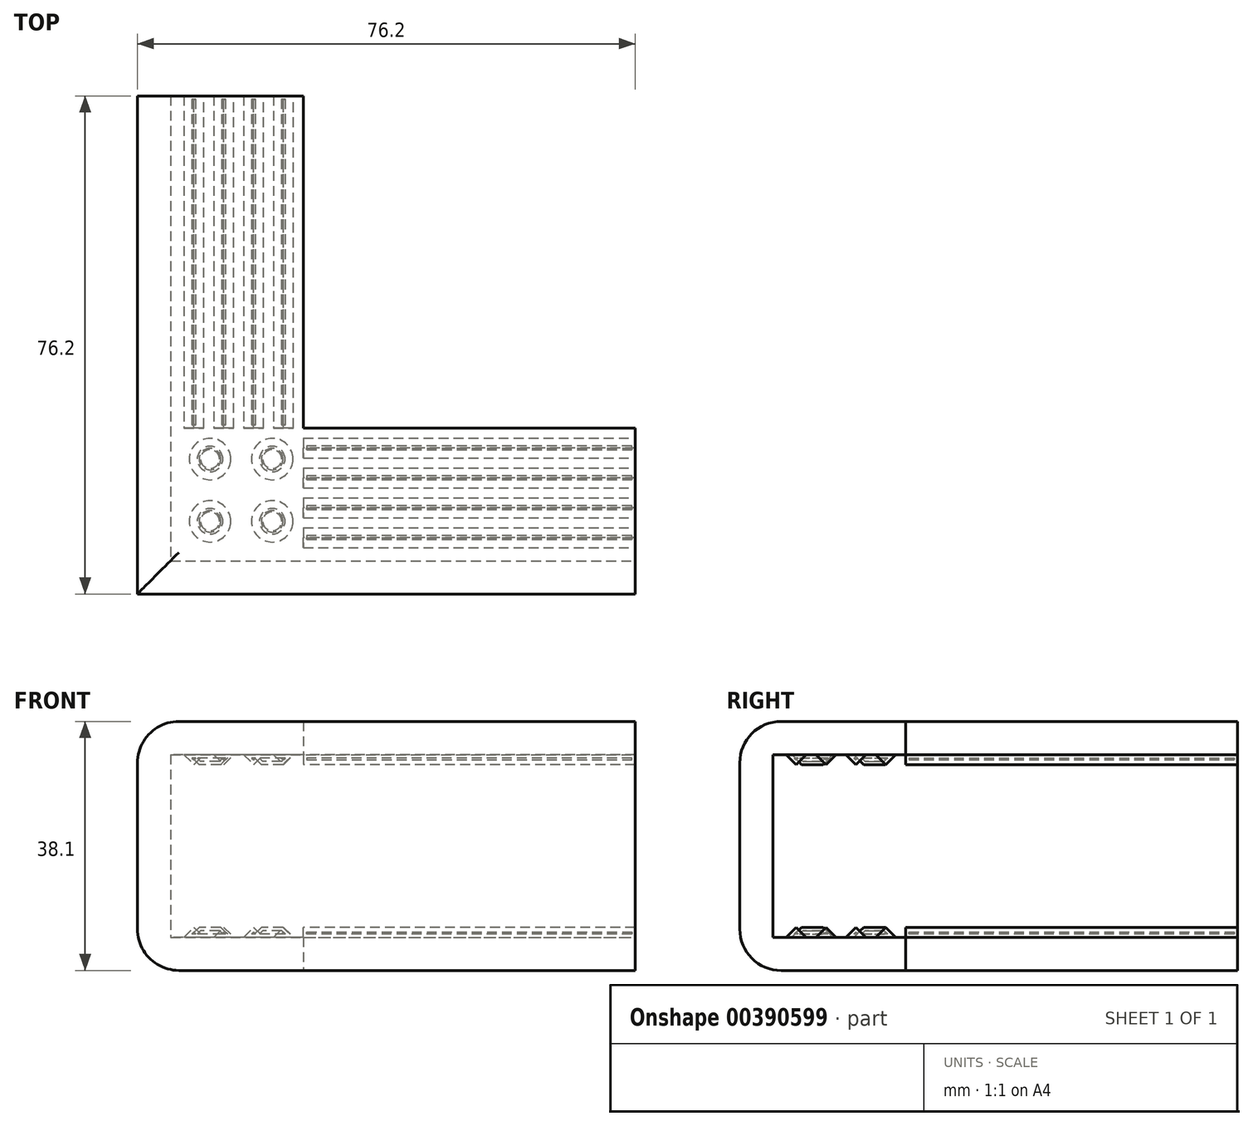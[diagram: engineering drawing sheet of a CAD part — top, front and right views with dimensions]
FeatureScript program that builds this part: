
annotation { "Feature Type Name" : "Feature", "Feature Type Description" : "" }
export const myFeature = defineFeature(function(context is Context, id is Id, definition is map)
    precondition{}
    {
        {
            var Q0;
            Q0=qCreatedBy(makeId("Top.planeOp"),FACE);
            var sketch = newSketch(context, id + "F0", { "sketchPlane" : qUnion([Q0])});
            skLineSegment(sketch, "E0", {"start": v(-49.11, 50.8) * mm, "end": v(-49.11, -25.4) * mm});
            skLineSegment(sketch, "E1", {"start": v(-49.11, -25.4) * mm, "end": v(27.09, -25.4) * mm});
            skLineSegment(sketch, "E2", {"start": v(27.09, -25.4) * mm, "end": v(27.09, 0) * mm});
            skLineSegment(sketch, "E3", {"start": v(27.09, 0) * mm, "end": v(-23.71, 0) * mm});
            skLineSegment(sketch, "E4", {"start": v(-23.71, 0) * mm, "end": v(-23.71, 50.8) * mm});
            skLineSegment(sketch, "E5", {"start": v(-23.71, 50.8) * mm, "end": v(-49.11, 50.8) * mm});
            skSolve(sketch);
        }
        {
            var Q0;
            Q0=makeQuery(id+"F0.imprint","IMPRINT",FACE,{"disambiguationData":[TD([[makeQuery(id+"F0.imprint","IMPRINT",EDGE,{"derivedFrom":sQuery(id+"F0.wireOp",EDGE,"E0")}),1.0]])]});
            extrude(context, id + "F1", {"entities" : qUnion([Q0]), "depth" : 38.1 * mm});
        }
        {
            var Q0;
            Q0=makeQuery(id+"F1.opExtrude","SWEPT_FACE",FACE,{"disambiguationData":[OSD([sQuery(id+"F0.wireOp",EDGE,"E3")])]});
            var Q1;
            Q1=makeQuery(id+"F1.opExtrude","SWEPT_FACE",FACE,{"disambiguationData":[OSD([sQuery(id+"F0.wireOp",EDGE,"E4")])]});
            var Q2;
            Q2=makeQuery(id+"F1.opExtrude","SWEPT_FACE",FACE,{"disambiguationData":[OSD([sQuery(id+"F0.wireOp",EDGE,"E2")])]});
            var Q3;
            Q3=makeQuery(id+"F1.opExtrude","SWEPT_FACE",FACE,{"disambiguationData":[OSD([sQuery(id+"F0.wireOp",EDGE,"E5")])]});
            shell(context, id + "F2", {"entities" : qUnion([Q0, Q1, Q2, Q3]), "thickness" : 5.08 * mm});
        }
        {
            var Q0;
            Q0=makeQuery(id+"F1.opExtrude","CAP_EDGE",EDGE,{"disambiguationData":[OSD([sQuery(id+"F0.wireOp",EDGE,"E1")])],"isStart":false});
            var Q1;
            Q1=makeQuery(id+"F1.opExtrude","CAP_EDGE",EDGE,{"disambiguationData":[OSD([sQuery(id+"F0.wireOp",EDGE,"E0")])],"isStart":false});
            fillet(context, id + "F3", {"entities" : qUnion([Q0, Q1]), "radius" : 6.35 * mm, "tangentPropagation" : true, "allowEdgeOverflow" : false});
        }
        {
            var Q0;
            Q0=makeQuery(id+"F1.opExtrude","CAP_EDGE",EDGE,{"disambiguationData":[OSD([sQuery(id+"F0.wireOp",EDGE,"E0")])],"isStart":true});
            var Q1;
            Q1=makeQuery(id+"F1.opExtrude","CAP_EDGE",EDGE,{"disambiguationData":[OSD([sQuery(id+"F0.wireOp",EDGE,"E1")])],"isStart":true});
            fillet(context, id + "F4", {"entities" : qUnion([Q0, Q1]), "radius" : 6.35 * mm, "tangentPropagation" : true, "allowEdgeOverflow" : false});
        }
        {
            var Q0;
            {var subQ0=sQuery(id+"F0.wireOp",EDGE,"E5");var subQ1=sQuery(id+"F0.wireOp",EDGE,"E4");var subQ2=sQuery(id+"F0.wireOp",EDGE,"E3");var subQ3=sQuery(id+"F0.wireOp",EDGE,"E2");var subQ4=sQuery(id+"F0.wireOp",EDGE,"E1");var subQ5=sQuery(id+"F0.wireOp",EDGE,"E0");Q0=makeQuery(id+"F2.opShell","OFFSET_FACE",FACE,{"disambiguationData":[OSD([subQ5,subQ4,subQ3,subQ2,subQ1,subQ0]),TDD([makeQuery(id+"F1.opExtrude","CAP_FACE",FACE,{"disambiguationData":[OSD([subQ5,subQ4,subQ3,subQ2,subQ1,subQ0])],"isStart":true})])]});}
            var sketch = newSketch(context, id + "F5", { "sketchPlane" : qUnion([Q0])});
            skLineSegment(sketch, "E6", {"start": v(-28.29, 50.8) * mm, "end": v(-25.24, 50.8) * mm});
            skLineSegment(sketch, "E7", {"start": v(-28.29, 50.8) * mm, "end": v(-28.29, 0) * mm});
            skLineSegment(sketch, "E8", {"start": v(-28.29, 0) * mm, "end": v(-25.24, 0) * mm});
            skLineSegment(sketch, "E9", {"start": v(-25.24, 0) * mm, "end": v(-25.24, 50.8) * mm});
            skLineSegment(sketch, "E10.bottom", {"start": v(-23.71, -1.52) * mm, "end": v(27.09, -1.52) * mm});
            skLineSegment(sketch, "E10.top", {"start": v(-23.71, -4.57) * mm, "end": v(27.09, -4.57) * mm});
            skLineSegment(sketch, "E10.left", {"start": v(-23.71, -1.52) * mm, "end": v(-23.71, -4.57) * mm});
            skLineSegment(sketch, "E10.right", {"start": v(27.09, -1.52) * mm, "end": v(27.09, -4.57) * mm});
            skLineSegment(sketch, "E11.0.1.0", {"start": v(-23.71, -6.1) * mm, "end": v(27.09, -6.1) * mm});
            skLineSegment(sketch, "E11.0.1.1", {"start": v(27.09, -6.1) * mm, "end": v(27.09, -9.14) * mm});
            skLineSegment(sketch, "E11.0.1.2", {"start": v(-23.71, -6.1) * mm, "end": v(-23.71, -9.14) * mm});
            skLineSegment(sketch, "E11.0.1.3", {"start": v(-23.71, -9.14) * mm, "end": v(27.09, -9.14) * mm});
            skLineSegment(sketch, "E11.0.2.0", {"start": v(-23.71, -10.67) * mm, "end": v(27.09, -10.67) * mm});
            skLineSegment(sketch, "E11.0.2.1", {"start": v(27.09, -10.67) * mm, "end": v(27.09, -13.72) * mm});
            skLineSegment(sketch, "E11.0.2.2", {"start": v(-23.71, -10.67) * mm, "end": v(-23.71, -13.72) * mm});
            skLineSegment(sketch, "E11.0.2.3", {"start": v(-23.71, -13.72) * mm, "end": v(27.09, -13.72) * mm});
            skLineSegment(sketch, "E11.0.3.0", {"start": v(-23.71, -15.24) * mm, "end": v(27.09, -15.24) * mm});
            skLineSegment(sketch, "E11.0.3.1", {"start": v(27.09, -15.24) * mm, "end": v(27.09, -18.29) * mm});
            skLineSegment(sketch, "E11.0.3.2", {"start": v(-23.71, -15.24) * mm, "end": v(-23.71, -18.29) * mm});
            skLineSegment(sketch, "E11.0.3.3", {"start": v(-23.71, -18.29) * mm, "end": v(27.09, -18.29) * mm});
            skLineSegment(sketch, "E11.direction1", {"start": v(-23.72, -4.57) * mm, "end": v(-23.71, -4.57) * mm, "construction": true});
            skLineSegment(sketch, "E11.direction2", {"start": v(-23.71, -4.57) * mm, "end": v(-23.71, -9.14) * mm, "construction": true});
            skLineSegment(sketch, "E12.1.0.0", {"start": v(-32.86, 50.8) * mm, "end": v(-29.8, 50.8) * mm});
            skLineSegment(sketch, "E12.1.0.1", {"start": v(-32.86, 50.8) * mm, "end": v(-32.86, 0) * mm});
            skLineSegment(sketch, "E12.1.0.2", {"start": v(-32.86, 0) * mm, "end": v(-29.8, 0) * mm});
            skLineSegment(sketch, "E12.1.0.3", {"start": v(-29.8, 0) * mm, "end": v(-29.8, 50.8) * mm});
            skLineSegment(sketch, "E12.2.0.0", {"start": v(-37.43, 50.8) * mm, "end": v(-34.38, 50.8) * mm});
            skLineSegment(sketch, "E12.2.0.1", {"start": v(-37.43, 50.8) * mm, "end": v(-37.43, 0) * mm});
            skLineSegment(sketch, "E12.2.0.2", {"start": v(-37.43, 0) * mm, "end": v(-34.38, 0) * mm});
            skLineSegment(sketch, "E12.2.0.3", {"start": v(-34.38, 0) * mm, "end": v(-34.38, 50.8) * mm});
            skLineSegment(sketch, "E12.3.0.0", {"start": v(-42, 50.8) * mm, "end": v(-38.95, 50.8) * mm});
            skLineSegment(sketch, "E12.3.0.1", {"start": v(-42, 50.8) * mm, "end": v(-42, 0) * mm});
            skLineSegment(sketch, "E12.3.0.2", {"start": v(-42, 0) * mm, "end": v(-38.95, 0) * mm});
            skLineSegment(sketch, "E12.3.0.3", {"start": v(-38.95, 0) * mm, "end": v(-38.95, 50.8) * mm});
            skLineSegment(sketch, "E12.direction1", {"start": v(-28.29, 0) * mm, "end": v(-32.86, 0) * mm, "construction": true});
            skCircle(sketch, "E13", {"center": v(-38, -4.76) * mm, "radius": 3.18 * mm});
            skCircle(sketch, "E14.0.1.0", {"center": v(-38, -14.29) * mm, "radius": 3.18 * mm});
            skCircle(sketch, "E14.1.0.0", {"center": v(-28.48, -4.76) * mm, "radius": 3.18 * mm});
            skCircle(sketch, "E14.1.1.0", {"center": v(-28.48, -14.29) * mm, "radius": 3.18 * mm});
            skLineSegment(sketch, "E14.direction1", {"start": v(-38, -4.76) * mm, "end": v(-28.48, -4.76) * mm, "construction": true});
            skLineSegment(sketch, "E14.direction2", {"start": v(-38, -4.76) * mm, "end": v(-38, -14.29) * mm, "construction": true});
            skLineSegment(sketch, "E15.0.0", {"start": v(-23.71, 50.8) * mm, "end": v(-23.71, 0) * mm});
            skLineSegment(sketch, "E15.0.1", {"start": v(-23.71, 0) * mm, "end": v(27.09, 0) * mm});
            skLineSegment(sketch, "E15.0.2", {"start": v(27.09, 0) * mm, "end": v(27.09, -20.32) * mm});
            skLineSegment(sketch, "E15.0.3", {"start": v(27.09, -20.32) * mm, "end": v(-44.03, -20.32) * mm});
            skLineSegment(sketch, "E15.0.4", {"start": v(-44.03, -20.32) * mm, "end": v(-44.03, 50.8) * mm});
            skLineSegment(sketch, "E15.0.5", {"start": v(-44.03, 50.8) * mm, "end": v(-23.71, 50.8) * mm});
            skLineSegment(sketch, "E16.0", {"start": v(-23.71, 0) * mm, "end": v(-23.71, 50.8) * mm});
            skLineSegment(sketch, "E16.1", {"start": v(27.09, 0) * mm, "end": v(-23.71, 0) * mm});
            skSolve(sketch);
        }
        {
            var Q0;
            {var subQ0=sQuery(id+"F5.wireOp",EDGE,"E10.bottom");Q0=makeQuery(id+"F5.imprint","IMPRINT",FACE,{"disambiguationData":[TD([[makeQuery(id+"F5.imprint","IMPRINT",EDGE,{"derivedFrom":subQ0}),-1.0]])]});}
            var Q1;
            {var subQ0=sQuery(id+"F5.wireOp",EDGE,"E11.0.1.0");Q1=makeQuery(id+"F5.imprint","IMPRINT",FACE,{"disambiguationData":[TD([[makeQuery(id+"F5.imprint","IMPRINT",EDGE,{"derivedFrom":subQ0}),-1.0]])]});}
            var Q2;
            {var subQ0=sQuery(id+"F5.wireOp",EDGE,"E11.0.2.0");Q2=makeQuery(id+"F5.imprint","IMPRINT",FACE,{"disambiguationData":[TD([[makeQuery(id+"F5.imprint","IMPRINT",EDGE,{"derivedFrom":subQ0}),-1.0]])]});}
            var Q3;
            {var subQ0=sQuery(id+"F5.wireOp",EDGE,"E11.0.3.0");Q3=makeQuery(id+"F5.imprint","IMPRINT",FACE,{"disambiguationData":[TD([[makeQuery(id+"F5.imprint","IMPRINT",EDGE,{"derivedFrom":subQ0}),-1.0]])]});}
            var Q4;
            Q4=makeQuery(id+"F5.imprint","IMPRINT",FACE,{"disambiguationData":[TD([[makeQuery(id+"F5.imprint","IMPRINT",EDGE,{"derivedFrom":sQuery(id+"F5.wireOp",EDGE,"E14.0.1.0")}),1.0]])]});
            var Q5;
            {var subQ0=sQuery(id+"F5.wireOp",EDGE,"E12.3.0.1");Q5=makeQuery(id+"F5.imprint","IMPRINT",FACE,{"disambiguationData":[TD([[makeQuery(id+"F5.imprint","IMPRINT",EDGE,{"derivedFrom":subQ0}),1.0]])]});}
            var Q6;
            {var subQ0=sQuery(id+"F5.wireOp",EDGE,"E12.2.0.1");Q6=makeQuery(id+"F5.imprint","IMPRINT",FACE,{"disambiguationData":[TD([[makeQuery(id+"F5.imprint","IMPRINT",EDGE,{"derivedFrom":subQ0}),1.0]])]});}
            var Q7;
            {var subQ0=sQuery(id+"F5.wireOp",EDGE,"E12.1.0.1");Q7=makeQuery(id+"F5.imprint","IMPRINT",FACE,{"disambiguationData":[TD([[makeQuery(id+"F5.imprint","IMPRINT",EDGE,{"derivedFrom":subQ0}),1.0]])]});}
            var Q8;
            {var subQ0=sQuery(id+"F5.wireOp",EDGE,"E7");Q8=makeQuery(id+"F5.imprint","IMPRINT",FACE,{"disambiguationData":[TD([[makeQuery(id+"F5.imprint","IMPRINT",EDGE,{"derivedFrom":subQ0}),1.0]])]});}
            var Q9;
            Q9=makeQuery(id+"F5.imprint","IMPRINT",FACE,{"disambiguationData":[TD([[makeQuery(id+"F5.imprint","IMPRINT",EDGE,{"derivedFrom":sQuery(id+"F5.wireOp",EDGE,"E14.1.0.0")}),1.0]])]});
            var Q10;
            Q10=makeQuery(id+"F5.imprint","IMPRINT",FACE,{"disambiguationData":[TD([[makeQuery(id+"F5.imprint","IMPRINT",EDGE,{"derivedFrom":sQuery(id+"F5.wireOp",EDGE,"E13")}),1.0]])]});
            var Q11;
            Q11=makeQuery(id+"F5.imprint","IMPRINT",FACE,{"disambiguationData":[TD([[makeQuery(id+"F5.imprint","IMPRINT",EDGE,{"derivedFrom":sQuery(id+"F5.wireOp",EDGE,"E14.1.1.0")}),1.0]])]});
            extrude(context, id + "F6", {"entities" : qUnion([Q0, Q1, Q2, Q3, Q4, Q5, Q6, Q7, Q8, Q9, Q10, Q11]), "depth" : 1.52 * mm});
        }
        {
            var Q0;
            Q0=makeQuery(id+"F6.opExtrude","CAP_EDGE",EDGE,{"disambiguationData":[OSD([sQuery(id+"F5.wireOp",EDGE,"E13")])],"isStart":false});
            var Q1;
            Q1=makeQuery(id+"F6.opExtrude","CAP_EDGE",EDGE,{"disambiguationData":[OSD([sQuery(id+"F5.wireOp",EDGE,"E14.1.0.0")])],"isStart":false});
            var Q2;
            Q2=makeQuery(id+"F6.opExtrude","CAP_EDGE",EDGE,{"disambiguationData":[OSD([sQuery(id+"F5.wireOp",EDGE,"E14.0.1.0")])],"isStart":false});
            var Q3;
            Q3=makeQuery(id+"F6.opExtrude","CAP_EDGE",EDGE,{"disambiguationData":[OSD([sQuery(id+"F5.wireOp",EDGE,"E14.1.1.0")])],"isStart":false});
            var Q4;
            Q4=makeQuery(id+"F6.opExtrude","CAP_EDGE",EDGE,{"disambiguationData":[OSD([sQuery(id+"F5.wireOp",EDGE,"E11.0.3.3")])],"isStart":false});
            var Q5;
            Q5=makeQuery(id+"F6.opExtrude","CAP_EDGE",EDGE,{"disambiguationData":[OSD([sQuery(id+"F5.wireOp",EDGE,"E11.0.3.0")])],"isStart":false});
            var Q6;
            Q6=makeQuery(id+"F6.opExtrude","CAP_EDGE",EDGE,{"disambiguationData":[OSD([sQuery(id+"F5.wireOp",EDGE,"E11.0.2.3")])],"isStart":false});
            var Q7;
            Q7=makeQuery(id+"F6.opExtrude","CAP_EDGE",EDGE,{"disambiguationData":[OSD([sQuery(id+"F5.wireOp",EDGE,"E11.0.2.0")])],"isStart":false});
            var Q8;
            Q8=makeQuery(id+"F6.opExtrude","CAP_EDGE",EDGE,{"disambiguationData":[OSD([sQuery(id+"F5.wireOp",EDGE,"E11.0.1.3")])],"isStart":false});
            var Q9;
            Q9=makeQuery(id+"F6.opExtrude","CAP_EDGE",EDGE,{"disambiguationData":[OSD([sQuery(id+"F5.wireOp",EDGE,"E11.0.1.0")])],"isStart":false});
            var Q10;
            Q10=makeQuery(id+"F6.opExtrude","CAP_EDGE",EDGE,{"disambiguationData":[OSD([sQuery(id+"F5.wireOp",EDGE,"E10.top")])],"isStart":false});
            var Q11;
            Q11=makeQuery(id+"F6.opExtrude","CAP_EDGE",EDGE,{"disambiguationData":[OSD([sQuery(id+"F5.wireOp",EDGE,"E10.bottom")])],"isStart":false});
            var Q12;
            Q12=makeQuery(id+"F6.opExtrude","CAP_EDGE",EDGE,{"disambiguationData":[OSD([sQuery(id+"F5.wireOp",EDGE,"E9")])],"isStart":false});
            var Q13;
            Q13=makeQuery(id+"F6.opExtrude","CAP_EDGE",EDGE,{"disambiguationData":[OSD([sQuery(id+"F5.wireOp",EDGE,"E7")])],"isStart":false});
            var Q14;
            Q14=makeQuery(id+"F6.opExtrude","CAP_EDGE",EDGE,{"disambiguationData":[OSD([sQuery(id+"F5.wireOp",EDGE,"E12.1.0.3")])],"isStart":false});
            var Q15;
            Q15=makeQuery(id+"F6.opExtrude","CAP_EDGE",EDGE,{"disambiguationData":[OSD([sQuery(id+"F5.wireOp",EDGE,"E12.1.0.1")])],"isStart":false});
            var Q16;
            Q16=makeQuery(id+"F6.opExtrude","CAP_EDGE",EDGE,{"disambiguationData":[OSD([sQuery(id+"F5.wireOp",EDGE,"E12.2.0.3")])],"isStart":false});
            var Q17;
            Q17=makeQuery(id+"F6.opExtrude","CAP_EDGE",EDGE,{"disambiguationData":[OSD([sQuery(id+"F5.wireOp",EDGE,"E12.2.0.1")])],"isStart":false});
            var Q18;
            Q18=makeQuery(id+"F6.opExtrude","CAP_EDGE",EDGE,{"disambiguationData":[OSD([sQuery(id+"F5.wireOp",EDGE,"E12.3.0.3")])],"isStart":false});
            var Q19;
            Q19=makeQuery(id+"F6.opExtrude","CAP_EDGE",EDGE,{"disambiguationData":[OSD([sQuery(id+"F5.wireOp",EDGE,"E12.3.0.1")])],"isStart":false});
            chamfer(context, id + "F7", {"entities" : qUnion([Q0, Q1, Q2, Q3, Q4, Q5, Q6, Q7, Q8, Q9, Q10, Q11, Q12, Q13, Q14, Q15, Q16, Q17, Q18, Q19]), "width" : 1.52 * mm, "tangentPropagation" : true});
        }
        {
            var Q0;
            Q0=makeQuery(id+"F6.opExtrude","CAP_FACE",FACE,{"disambiguationData":[OSD([sQuery(id+"F5.wireOp",EDGE,"E10.bottom"),sQuery(id+"F5.wireOp",EDGE,"E10.top"),sQuery(id+"F5.wireOp",EDGE,"E10.left"),sQuery(id+"F5.wireOp",EDGE,"E15.0.2")])],"isStart":false});
            var Q1;
            Q1=makeQuery(id+"F6.opExtrude","CAP_FACE",FACE,{"disambiguationData":[OSD([sQuery(id+"F5.wireOp",EDGE,"E11.0.1.0"),sQuery(id+"F5.wireOp",EDGE,"E11.0.1.2"),sQuery(id+"F5.wireOp",EDGE,"E11.0.1.3"),sQuery(id+"F5.wireOp",EDGE,"E15.0.2")])],"isStart":false});
            var Q2;
            Q2=makeQuery(id+"F6.opExtrude","CAP_FACE",FACE,{"disambiguationData":[OSD([sQuery(id+"F5.wireOp",EDGE,"E11.0.2.0"),sQuery(id+"F5.wireOp",EDGE,"E11.0.2.2"),sQuery(id+"F5.wireOp",EDGE,"E11.0.2.3"),sQuery(id+"F5.wireOp",EDGE,"E15.0.2")])],"isStart":false});
            var Q3;
            Q3=makeQuery(id+"F6.opExtrude","CAP_FACE",FACE,{"disambiguationData":[OSD([sQuery(id+"F5.wireOp",EDGE,"E11.0.3.0"),sQuery(id+"F5.wireOp",EDGE,"E11.0.3.2"),sQuery(id+"F5.wireOp",EDGE,"E11.0.3.3"),sQuery(id+"F5.wireOp",EDGE,"E15.0.2")])],"isStart":false});
            var Q4;
            Q4=makeQuery(id+"F6.opExtrude","CAP_FACE",FACE,{"disambiguationData":[OSD([sQuery(id+"F5.wireOp",EDGE,"E14.1.1.0")])],"isStart":false});
            var Q5;
            Q5=makeQuery(id+"F6.opExtrude","CAP_FACE",FACE,{"disambiguationData":[OSD([sQuery(id+"F5.wireOp",EDGE,"E14.0.1.0")])],"isStart":false});
            var Q6;
            Q6=makeQuery(id+"F6.opExtrude","CAP_FACE",FACE,{"disambiguationData":[OSD([sQuery(id+"F5.wireOp",EDGE,"E14.1.0.0")])],"isStart":false});
            var Q7;
            Q7=makeQuery(id+"F6.opExtrude","CAP_FACE",FACE,{"disambiguationData":[OSD([sQuery(id+"F5.wireOp",EDGE,"E13")])],"isStart":false});
            var Q8;
            Q8=makeQuery(id+"F6.opExtrude","CAP_FACE",FACE,{"disambiguationData":[OSD([sQuery(id+"F5.wireOp",EDGE,"E7"),sQuery(id+"F5.wireOp",EDGE,"E8"),sQuery(id+"F5.wireOp",EDGE,"E9"),sQuery(id+"F5.wireOp",EDGE,"E15.0.5")])],"isStart":false});
            var Q9;
            Q9=makeQuery(id+"F6.opExtrude","CAP_FACE",FACE,{"disambiguationData":[OSD([sQuery(id+"F5.wireOp",EDGE,"E12.1.0.1"),sQuery(id+"F5.wireOp",EDGE,"E12.1.0.2"),sQuery(id+"F5.wireOp",EDGE,"E12.1.0.3"),sQuery(id+"F5.wireOp",EDGE,"E15.0.5")])],"isStart":false});
            var Q10;
            Q10=makeQuery(id+"F6.opExtrude","CAP_FACE",FACE,{"disambiguationData":[OSD([sQuery(id+"F5.wireOp",EDGE,"E12.2.0.1"),sQuery(id+"F5.wireOp",EDGE,"E12.2.0.2"),sQuery(id+"F5.wireOp",EDGE,"E12.2.0.3"),sQuery(id+"F5.wireOp",EDGE,"E15.0.5")])],"isStart":false});
            var Q11;
            Q11=makeQuery(id+"F6.opExtrude","CAP_FACE",FACE,{"disambiguationData":[OSD([sQuery(id+"F5.wireOp",EDGE,"E12.3.0.1"),sQuery(id+"F5.wireOp",EDGE,"E12.3.0.2"),sQuery(id+"F5.wireOp",EDGE,"E12.3.0.3"),sQuery(id+"F5.wireOp",EDGE,"E15.0.5")])],"isStart":false});
            var Q12;
            Q12=makeQuery(id+"F6.opExtrude","SWEPT_BODY",BODY,{"disambiguationData":[OSD([sQuery(id+"F5.wireOp",EDGE,"E10.bottom"),sQuery(id+"F5.wireOp",EDGE,"E10.top"),sQuery(id+"F5.wireOp",EDGE,"E10.left"),sQuery(id+"F5.wireOp",EDGE,"E15.0.2")])]});
            var Q13;
            Q13=makeQuery(id+"F6.opExtrude","SWEPT_BODY",BODY,{"disambiguationData":[OSD([sQuery(id+"F5.wireOp",EDGE,"E14.1.1.0")])]});
            var Q14;
            Q14=makeQuery(id+"F6.opExtrude","SWEPT_BODY",BODY,{"disambiguationData":[OSD([sQuery(id+"F5.wireOp",EDGE,"E14.0.1.0")])]});
            var Q15;
            Q15=makeQuery(id+"F6.opExtrude","SWEPT_BODY",BODY,{"disambiguationData":[OSD([sQuery(id+"F5.wireOp",EDGE,"E13")])]});
            var Q16;
            Q16=makeQuery(id+"F6.opExtrude","SWEPT_BODY",BODY,{"disambiguationData":[OSD([sQuery(id+"F5.wireOp",EDGE,"E14.1.0.0")])]});
            var Q17;
            Q17=makeQuery(id+"F6.opExtrude","SWEPT_BODY",BODY,{"disambiguationData":[OSD([sQuery(id+"F5.wireOp",EDGE,"E11.0.1.0"),sQuery(id+"F5.wireOp",EDGE,"E11.0.1.2"),sQuery(id+"F5.wireOp",EDGE,"E11.0.1.3"),sQuery(id+"F5.wireOp",EDGE,"E15.0.2")])]});
            var Q18;
            Q18=makeQuery(id+"F6.opExtrude","SWEPT_BODY",BODY,{"disambiguationData":[OSD([sQuery(id+"F5.wireOp",EDGE,"E11.0.2.0"),sQuery(id+"F5.wireOp",EDGE,"E11.0.2.2"),sQuery(id+"F5.wireOp",EDGE,"E11.0.2.3"),sQuery(id+"F5.wireOp",EDGE,"E15.0.2")])]});
            var Q19;
            Q19=makeQuery(id+"F6.opExtrude","SWEPT_BODY",BODY,{"disambiguationData":[OSD([sQuery(id+"F5.wireOp",EDGE,"E11.0.3.0"),sQuery(id+"F5.wireOp",EDGE,"E11.0.3.2"),sQuery(id+"F5.wireOp",EDGE,"E11.0.3.3"),sQuery(id+"F5.wireOp",EDGE,"E15.0.2")])]});
            var Q20;
            Q20=makeQuery(id+"F6.opExtrude","SWEPT_BODY",BODY,{"disambiguationData":[OSD([sQuery(id+"F5.wireOp",EDGE,"E7"),sQuery(id+"F5.wireOp",EDGE,"E8"),sQuery(id+"F5.wireOp",EDGE,"E9"),sQuery(id+"F5.wireOp",EDGE,"E15.0.5")])]});
            var Q21;
            Q21=makeQuery(id+"F6.opExtrude","SWEPT_BODY",BODY,{"disambiguationData":[OSD([sQuery(id+"F5.wireOp",EDGE,"E12.1.0.1"),sQuery(id+"F5.wireOp",EDGE,"E12.1.0.2"),sQuery(id+"F5.wireOp",EDGE,"E12.1.0.3"),sQuery(id+"F5.wireOp",EDGE,"E15.0.5")])]});
            var Q22;
            Q22=makeQuery(id+"F6.opExtrude","SWEPT_BODY",BODY,{"disambiguationData":[OSD([sQuery(id+"F5.wireOp",EDGE,"E12.2.0.1"),sQuery(id+"F5.wireOp",EDGE,"E12.2.0.2"),sQuery(id+"F5.wireOp",EDGE,"E12.2.0.3"),sQuery(id+"F5.wireOp",EDGE,"E15.0.5")])]});
            var Q23;
            Q23=makeQuery(id+"F6.opExtrude","SWEPT_BODY",BODY,{"disambiguationData":[OSD([sQuery(id+"F5.wireOp",EDGE,"E12.3.0.1"),sQuery(id+"F5.wireOp",EDGE,"E12.3.0.2"),sQuery(id+"F5.wireOp",EDGE,"E12.3.0.3"),sQuery(id+"F5.wireOp",EDGE,"E15.0.5")])]});
            shell(context, id + "F8", {"isHollow" : true, "entities" : qUnion([Q0, Q1, Q2, Q3, Q4, Q5, Q6, Q7, Q8, Q9, Q10, Q11]), "parts" : qUnion([Q12, Q13, Q14, Q15, Q16, Q17, Q18, Q19, Q20, Q21, Q22, Q23]), "thickness" : 0.5 * mm});
        }
        {
            var Q0;
            Q0=makeQuery(id+"F1.opExtrude","SWEPT_EDGE",EDGE,{"disambiguationData":[OSD([sQuery(id+"F0.wireOp",EDGE,"E1"),sQuery(id+"F0.wireOp",EDGE,"E2")])]});
            cPoint(context, id + "F9", {"entities" : qUnion([Q0]), "parameter" : 0.5});
        }
        {
            var Q0;
            Q0=makeQuery(id+"F2.opShell","OFFSET_EDGE",EDGE,{"disambiguationData":[OSD([sQuery(id+"F0.wireOp",EDGE,"E0"),sQuery(id+"F0.wireOp",EDGE,"E5")])]});
            cPoint(context, id + "F10", {"entities" : qUnion([Q0]), "parameter" : 0.5});
        }
        {
            var Q0;
            Q0=makeQuery(id+"F1.opExtrude","SWEPT_EDGE",EDGE,{"disambiguationData":[OSD([sQuery(id+"F0.wireOp",EDGE,"E0"),sQuery(id+"F0.wireOp",EDGE,"E1")])]});
            cPoint(context, id + "F11", {"entities" : qUnion([Q0]), "parameter" : 0.5});
        }
        {
            var Q0;
            Q0 = qCreatedBy(id + "F9" ,VERTEX);
            var Q1;
            Q1 = qCreatedBy(id + "F10" ,VERTEX);
            var Q2;
            Q2 = qCreatedBy(id + "F11" ,VERTEX);
            cPlane(context, id + "F12", {"entities" : qUnion([Q0, Q1, Q2]), "cplaneType" : CPlaneType.THREE_POINT, "offset" : 25.4 * mm, "width" : 152.4 * mm, "height" : 152.4 * mm});
        }
        {
            var Q0;
            Q0=makeQuery(id+"F1.opExtrude","SWEPT_BODY",BODY,{"disambiguationData":[OSD([sQuery(id+"F0.wireOp",EDGE,"E0"),sQuery(id+"F0.wireOp",EDGE,"E1"),sQuery(id+"F0.wireOp",EDGE,"E2"),sQuery(id+"F0.wireOp",EDGE,"E3"),sQuery(id+"F0.wireOp",EDGE,"E4"),sQuery(id+"F0.wireOp",EDGE,"E5")])]});
            var Q1;
            Q1=makeQuery(id+"F6.opExtrude","SWEPT_BODY",BODY,{"disambiguationData":[OSD([sQuery(id+"F5.wireOp",EDGE,"E10.bottom"),sQuery(id+"F5.wireOp",EDGE,"E10.top"),sQuery(id+"F5.wireOp",EDGE,"E10.left"),sQuery(id+"F5.wireOp",EDGE,"E15.0.2")])]});
            var Q2;
            Q2=makeQuery(id+"F6.opExtrude","SWEPT_BODY",BODY,{"disambiguationData":[OSD([sQuery(id+"F5.wireOp",EDGE,"E7"),sQuery(id+"F5.wireOp",EDGE,"E8"),sQuery(id+"F5.wireOp",EDGE,"E9"),sQuery(id+"F5.wireOp",EDGE,"E15.0.5")])]});
            var Q3;
            Q3=makeQuery(id+"F6.opExtrude","SWEPT_BODY",BODY,{"disambiguationData":[OSD([sQuery(id+"F5.wireOp",EDGE,"E14.1.0.0")])]});
            var Q4;
            Q4=makeQuery(id+"F6.opExtrude","SWEPT_BODY",BODY,{"disambiguationData":[OSD([sQuery(id+"F5.wireOp",EDGE,"E14.1.1.0")])]});
            var Q5;
            Q5=makeQuery(id+"F6.opExtrude","SWEPT_BODY",BODY,{"disambiguationData":[OSD([sQuery(id+"F5.wireOp",EDGE,"E11.0.3.0"),sQuery(id+"F5.wireOp",EDGE,"E11.0.3.2"),sQuery(id+"F5.wireOp",EDGE,"E11.0.3.3"),sQuery(id+"F5.wireOp",EDGE,"E15.0.2")])]});
            var Q6;
            Q6=makeQuery(id+"F6.opExtrude","SWEPT_BODY",BODY,{"disambiguationData":[OSD([sQuery(id+"F5.wireOp",EDGE,"E11.0.2.0"),sQuery(id+"F5.wireOp",EDGE,"E11.0.2.2"),sQuery(id+"F5.wireOp",EDGE,"E11.0.2.3"),sQuery(id+"F5.wireOp",EDGE,"E15.0.2")])]});
            var Q7;
            Q7=makeQuery(id+"F6.opExtrude","SWEPT_BODY",BODY,{"disambiguationData":[OSD([sQuery(id+"F5.wireOp",EDGE,"E11.0.1.0"),sQuery(id+"F5.wireOp",EDGE,"E11.0.1.2"),sQuery(id+"F5.wireOp",EDGE,"E11.0.1.3"),sQuery(id+"F5.wireOp",EDGE,"E15.0.2")])]});
            var Q8;
            Q8=makeQuery(id+"F6.opExtrude","SWEPT_BODY",BODY,{"disambiguationData":[OSD([sQuery(id+"F5.wireOp",EDGE,"E14.0.1.0")])]});
            var Q9;
            Q9=makeQuery(id+"F6.opExtrude","SWEPT_BODY",BODY,{"disambiguationData":[OSD([sQuery(id+"F5.wireOp",EDGE,"E13")])]});
            var Q10;
            Q10=makeQuery(id+"F6.opExtrude","SWEPT_BODY",BODY,{"disambiguationData":[OSD([sQuery(id+"F5.wireOp",EDGE,"E12.1.0.1"),sQuery(id+"F5.wireOp",EDGE,"E12.1.0.2"),sQuery(id+"F5.wireOp",EDGE,"E12.1.0.3"),sQuery(id+"F5.wireOp",EDGE,"E15.0.5")])]});
            var Q11;
            Q11=makeQuery(id+"F6.opExtrude","SWEPT_BODY",BODY,{"disambiguationData":[OSD([sQuery(id+"F5.wireOp",EDGE,"E12.2.0.1"),sQuery(id+"F5.wireOp",EDGE,"E12.2.0.2"),sQuery(id+"F5.wireOp",EDGE,"E12.2.0.3"),sQuery(id+"F5.wireOp",EDGE,"E15.0.5")])]});
            var Q12;
            Q12=makeQuery(id+"F6.opExtrude","SWEPT_BODY",BODY,{"disambiguationData":[OSD([sQuery(id+"F5.wireOp",EDGE,"E12.3.0.1"),sQuery(id+"F5.wireOp",EDGE,"E12.3.0.2"),sQuery(id+"F5.wireOp",EDGE,"E12.3.0.3"),sQuery(id+"F5.wireOp",EDGE,"E15.0.5")])]});
            var Q13;
            Q13=qCreatedBy(id+"F12.planeOp",FACE);
            mirror(context, id + "F13", {"entities" : qUnion([Q0, Q1, Q2, Q3, Q4, Q5, Q6, Q7, Q8, Q9, Q10, Q11, Q12]), "mirrorPlane" : qUnion([Q13])});
        }
    });
